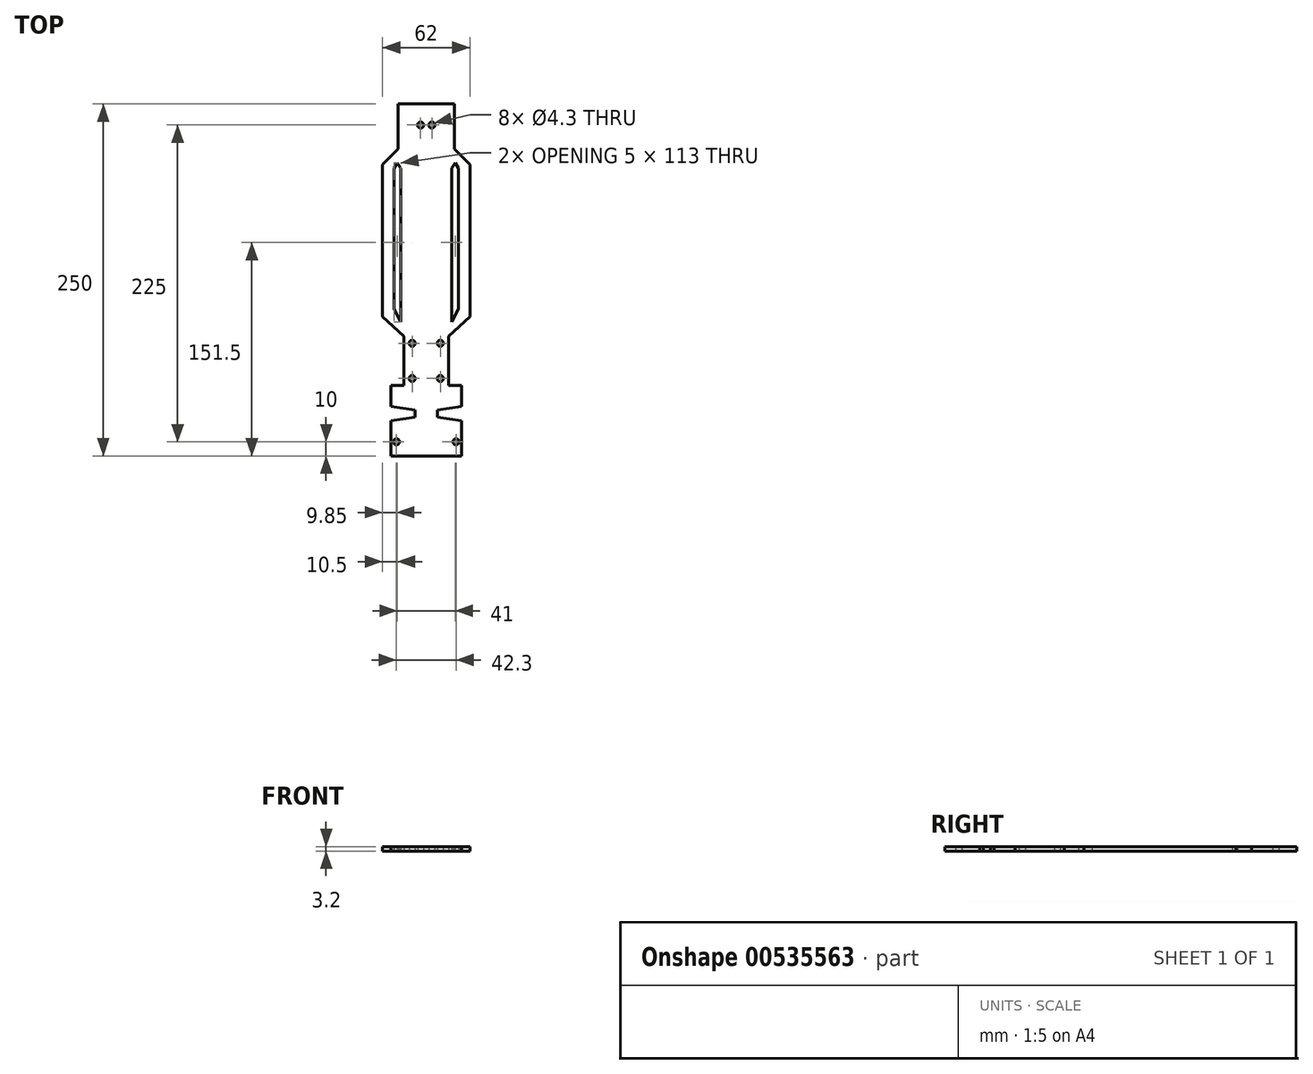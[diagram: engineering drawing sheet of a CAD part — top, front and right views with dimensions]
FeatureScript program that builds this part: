
annotation { "Feature Type Name" : "Feature", "Feature Type Description" : "" }
export const myFeature = defineFeature(function(context is Context, id is Id, definition is map)
    precondition{}
    {
        {
            var Q0;
            Q0=qCreatedBy(makeId("Top.planeOp"),FACE);
            var sketch = newSketch(context, id + "F0", { "sketchPlane" : qUnion([Q0])});
            skLineSegment(sketch, "E0.bottom", {"start": v(-25, -50) * mm, "end": v(25, -50) * mm});
            skLineSegment(sketch, "E0.top", {"start": v(-25, 0) * mm, "end": v(25, 0) * mm});
            skLineSegment(sketch, "E0.left", {"start": v(-25, -50) * mm, "end": v(-25, 0) * mm});
            skLineSegment(sketch, "E0.right", {"start": v(25, -50) * mm, "end": v(25, 0) * mm});
            skCircle(sketch, "E1", {"center": v(-21.15, -40) * mm, "radius": 2.15 * mm});
            skCircle(sketch, "E2.MirrorC", {"center": v(21.15, -40) * mm, "radius": 2.15 * mm});
            skLineSegment(sketch, "E3", {"start": v(-8, -17.5) * mm, "end": v(-8, -22.5) * mm});
            skLineSegment(sketch, "E4", {"start": v(-8, -22.5) * mm, "end": v(-25, -25) * mm});
            skLineSegment(sketch, "E5", {"start": v(-25, -25) * mm, "end": v(-25, -15) * mm});
            skLineSegment(sketch, "E6", {"start": v(-25, -15) * mm, "end": v(-8, -17.5) * mm});
            skLineSegment(sketch, "E7.MirrorCS", {"start": v(25, -15) * mm, "end": v(8, -17.5) * mm});
            skLineSegment(sketch, "E8.MirrorCS", {"start": v(8, -17.5) * mm, "end": v(8, -22.5) * mm});
            skLineSegment(sketch, "E9.MirrorCS", {"start": v(8, -22.5) * mm, "end": v(25, -25) * mm});
            skLineSegment(sketch, "E10.MirrorCS", {"start": v(25, -25) * mm, "end": v(25, -15) * mm});
            skLineSegment(sketch, "E11.bottom", {"start": v(-35, 0) * mm, "end": v(35, 0) * mm});
            skLineSegment(sketch, "E11.top", {"start": v(-35, 225) * mm, "end": v(35, 225) * mm});
            skLineSegment(sketch, "E11.left", {"start": v(-35, 0) * mm, "end": v(-35, 225) * mm});
            skLineSegment(sketch, "E11.right", {"start": v(35, 0) * mm, "end": v(35, 225) * mm});
            skCircle(sketch, "E12", {"center": v(-4, 185) * mm, "radius": 2.15 * mm});
            skCircle(sketch, "E13", {"center": v(4, 185) * mm, "radius": 2.15 * mm});
            skCircle(sketch, "E14", {"center": v(-10, 5) * mm, "radius": 2.15 * mm});
            skCircle(sketch, "E15", {"center": v(-10, 30) * mm, "radius": 2.15 * mm});
            skCircle(sketch, "E16.MirrorC", {"center": v(10, 30) * mm, "radius": 2.15 * mm});
            skCircle(sketch, "E17.MirrorC", {"center": v(10, 5) * mm, "radius": 2.15 * mm});
            skSolve(sketch);
        }
        {
            var Q0;
            {var subQ5=sQuery(id+"F0.wireOp",EDGE,"E0.bottom");Q0=makeQuery(id+"F0.imprint","IMPRINT",FACE,{"disambiguationData":[TD([[makeQuery(id+"F0.imprint","IMPRINT",EDGE,{"derivedFrom":subQ5}),1.0]])]});}
            var Q1;
            Q1=makeQuery(id+"F0.imprint","IMPRINT",FACE,{"disambiguationData":[TD([[makeQuery(id+"F0.imprint","IMPRINT",EDGE,{"derivedFrom":sQuery(id+"F0.wireOp",EDGE,"E11.top")}),-1.0]])]});
            extrude(context, id + "F1", {"entities" : qUnion([Q0, Q1]), "depth" : 3.2 * mm, "offsetDistance" : 25 * mm});
        }
        {
            var Q0;
            Q0=qCreatedBy(makeId("Top.planeOp"),FACE);
            var sketch = newSketch(context, id + "F2", { "sketchPlane" : qUnion([Q0])});
            skLineSegment(sketch, "E18", {"start": v(-20, 200) * mm, "end": v(20, 200) * mm});
            skLineSegment(sketch, "E19", {"start": v(20.63, 158) * mm, "end": v(18, 154.43) * mm});
            skLineSegment(sketch, "E20", {"start": v(16, 0) * mm, "end": v(31, 0) * mm});
            skLineSegment(sketch, "E21", {"start": v(31, 0) * mm, "end": v(31, 225) * mm});
            skLineSegment(sketch, "E22", {"start": v(31, 225) * mm, "end": v(-31, 225) * mm});
            skLineSegment(sketch, "E23.MirrorCS", {"start": v(-16, 0) * mm, "end": v(-31, 0) * mm});
            skLineSegment(sketch, "E24.MirrorCS", {"start": v(-31, 0) * mm, "end": v(-31, 225) * mm});
            skLineSegment(sketch, "E25.MirrorCS", {"start": v(-20.63, 158) * mm, "end": v(-18, 154.43) * mm});
            skLineSegment(sketch, "E26", {"start": v(-20.63, 158) * mm, "end": v(-23, 154.43) * mm});
            skLineSegment(sketch, "E27", {"start": v(-23, 154.43) * mm, "end": v(-23, 54.43) * mm});
            skLineSegment(sketch, "E28.MirrorCS", {"start": v(23, 54.43) * mm, "end": v(18, 45) * mm});
            skLineSegment(sketch, "E29.MirrorCS", {"start": v(23, 154.43) * mm, "end": v(23, 54.43) * mm});
            skLineSegment(sketch, "E30.MirrorCS", {"start": v(20.63, 158) * mm, "end": v(23, 154.43) * mm});
            skLineSegment(sketch, "E31", {"start": v(-20, 168) * mm, "end": v(-31, 157) * mm});
            skLineSegment(sketch, "E32", {"start": v(-31, 157) * mm, "end": v(-31, 49) * mm});
            skLineSegment(sketch, "E33", {"start": v(-31, 49) * mm, "end": v(-16, 35) * mm});
            skLineSegment(sketch, "E34.MirrorCS", {"start": v(31, 49) * mm, "end": v(16, 35) * mm});
            skLineSegment(sketch, "E35.MirrorCS", {"start": v(31, 157) * mm, "end": v(31, 49) * mm});
            skLineSegment(sketch, "E36.MirrorCS", {"start": v(20, 168) * mm, "end": v(31, 157) * mm});
            skLineSegment(sketch, "E37", {"start": v(-18, 154.43) * mm, "end": v(-18, 45) * mm});
            skLineSegment(sketch, "E38", {"start": v(18, 45) * mm, "end": v(18, 154.43) * mm});
            skLineSegment(sketch, "E39", {"start": v(16, 35) * mm, "end": v(16, 0) * mm});
            skLineSegment(sketch, "E40", {"start": v(-16, 35) * mm, "end": v(-16, 0) * mm});
            skLineSegment(sketch, "E41", {"start": v(-20, 200) * mm, "end": v(-20, 168) * mm});
            skLineSegment(sketch, "E42", {"start": v(20, 168) * mm, "end": v(20, 200) * mm});
            skLineSegment(sketch, "E43", {"start": v(-23, 54.43) * mm, "end": v(-18, 45) * mm});
            skLineSegment(sketch, "E44.bottom", {"start": v(-35, 0) * mm, "end": v(-31, 0) * mm});
            skLineSegment(sketch, "E44.top", {"start": v(-35, 225) * mm, "end": v(-31, 225) * mm});
            skLineSegment(sketch, "E44.left", {"start": v(-35, 0) * mm, "end": v(-35, 225) * mm});
            skLineSegment(sketch, "E45.bottom", {"start": v(35, 0) * mm, "end": v(31, 0) * mm});
            skLineSegment(sketch, "E45.top", {"start": v(35, 225) * mm, "end": v(31, 225) * mm});
            skLineSegment(sketch, "E45.left", {"start": v(35, 0) * mm, "end": v(35, 225) * mm});
            skSolve(sketch);
        }
        {
            var Q0;
            Q0 = qSketchRegion(id + "F2", true);
            extrude(context, id + "F3", {"entities" : qUnion([Q0]), "operationType" : NewBodyOperationType.REMOVE, "depth" : 74 * mm, "offsetDistance" : 25 * mm});
        }
        {
            var Q0;
            Q0 = qSketchRegion(id + "F2", true);
            extrude(context, id + "F4", {"entities" : qUnion([Q0]), "operationType" : NewBodyOperationType.REMOVE, "oppositeDirection" : true, "depth" : 32.4 * mm, "offsetDistance" : 25 * mm});
        }
    });
